# Revit family: Thorn OMEGA PRO 2
name_source: partatom
category: Lighting Fixtures
revit_build: Autodesk Revit 2016 (Build: 20150220_1215(x64)
units: mm (PartAtom-declared; Revit-internal decimal feet)

## family parameters
Cut with Voids When Loaded = No
Host = Face
Light Source = Yes
OmniClass Number = 23.80.70.11
OmniClass Title = Luminaries for Internal Lighting
Part Type = Normal
Room Calculation Point = No
Round Connector Dimension = Use Diameter
Shared = No

## types (7) — shared parameters
Assembly Code = D5020200
Body = ZG_Metal_White
Color Filter = 16777215
Cover = ZG_PMMA
Description = Recessed LED luminaire
Dimming Lamp Color Temperature Shift = <None>
Emit Shape Visible in Rendering = No
Lamp = LED
Manufacturer = Thorn Lighting
Tilt Angle = -90.00°
Voltage = 230 V
zero-valued in all types: Default Elevation

## per-type parameters (varying)
| type | Apparent Load | Emit from Rectangle Length | Emit from Rectangle Width | Height | Length | Model | No Sensor | Photometric Web File | Sensor | URL | Width |
| OP2 CKIT+ 3X12 | 24 VA | 249 mm | 1149 mm  [stored 3.76969 ft] | 59 mm | 1197 mm  [stored 3.92717 ft] | 96631596 | No | TLG_SP_0043991.IES | Yes | www.thornlighting.com/96633091 | 297 mm  [stored 0.974409 ft] |
| Q625 | 29 VA | 574 mm | 574 mm | 57 mm | 622 mm | 92914009 | Yes | TLG_SP_0043963.IES | No | www.thornlighting.com/92914009 | 622 mm |
| OP2 Q600 | 29 VA | 549 mm | 549 mm | 55 mm | 597 mm | 92913231 | Yes | TLG_SP_0043957.IES | No | www.thornlighting.com/92913231 | 597 mm |
| OP2 3X12 | 29 VA | 249 mm | 1149 mm  [stored 3.76969 ft] | 57 mm | 1197 mm  [stored 3.92717 ft] | 92914006 | Yes | TLG_SP_0043981.IES | No | www.thornlighting.com/92914006 | 297 mm  [stored 0.974409 ft] |
| OP2 CKIT+ Q625 | 29 VA | 574 mm | 574 mm | 57 mm | 622 mm | 96633089 | No | TLG_SP_0043975.IES | Yes | www.thornlighting.com/96633089 | 622 mm |
| OP2 CKIT+ Q600 | 29 VA | 549 mm | 549 mm | 57 mm | 597 mm | 96633086 | No | TLG_SP_0043969.IES | Yes | www.thornlighting.com/96633086 | 597 mm |
| OP2 HFIX - Q300 | 18 VA | 249 mm | 249 mm | 15 mm  [stored 0.0492126 ft] | 297 mm  [stored 0.974409 ft] | 96634417 | Yes | 96634417_(STD).IES | No | www.thornlighting.com/96634417 | 297 mm  [stored 0.974409 ft] |

note: [stored X ft] marks values corroborated as IEEE doubles in the binary element streams (Revit-internal decimal feet)

## geometry (parser evidence)
native form markers: Sweep x3
no freeform markers — native parametric forms only
